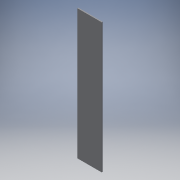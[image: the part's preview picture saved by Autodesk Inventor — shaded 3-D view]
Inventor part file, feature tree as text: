
AUTODESK INVENTOR PART (.ipt)
format: ipt  version: 2019 (Build 230136000, 136)  size: 91,648 bytes
history: native  units: in
note: dims shown in document units (in); Inventor stores cm internally (conversion verified against a paired STEP export)
features: other x2, extrude x1, sketch x1, reference x1
ambient origin geometry x8: Origin, YZ Plane, XZ Plane, XY Plane, X Axis, Y Axis, Z Axis, Center Point
bodies: Solid1 (feature_tree)
feature tree (5):
  extrude  "Extrusion1"  Depth=0.75in TaperAngle=0.0deg
  sketch  "Sketch1"  dims[d0=18.0in d1=0.75in d2=0.0in]
  reference  "Reference1"
  other  "Assembly4"
  other  "Side1:1"
